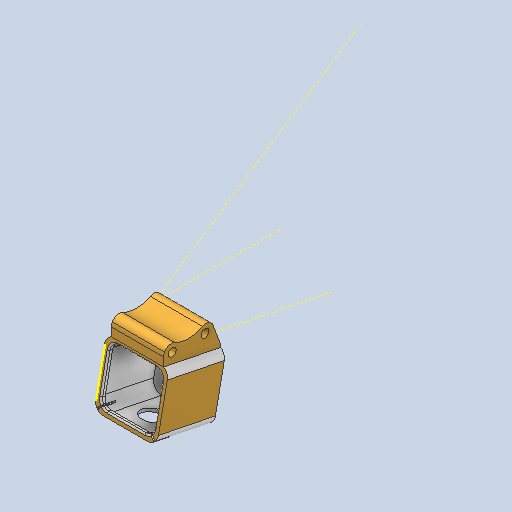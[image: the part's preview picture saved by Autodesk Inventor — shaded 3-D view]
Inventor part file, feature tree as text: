
AUTODESK INVENTOR PART (.ipt)
format: ipt  version: 2023 (Build 270158000, 158)  size: 250,880 bytes
history: native  units: mm
features: other x3, sketch x3, projected_geometry x2, extrude x1
ambient origin geometry x8: Origin, YZ Plane, XZ Plane, XY Plane, X Axis, Y Axis, Z Axis, Center Point
bodies: Solid1 (feature_tree)
feature tree (9):
  other  "V2 modular session template.iam"
  other  "V2 modular session camera case.ipt:1"
  other  "V2 modular session frame mount.ipt:1"
  extrude  "Extrusion1"  Depth=10.0mm TaperAngle=0.0deg
  sketch  "Sketch6"
  sketch  "Sketch7"
  sketch  "Sketch3"  dims[d0=10.0mm d1=10.0mm d2=0.0mm]
  projected_geometry  "Projected Loop1"
  projected_geometry  "Projected Loop2"
